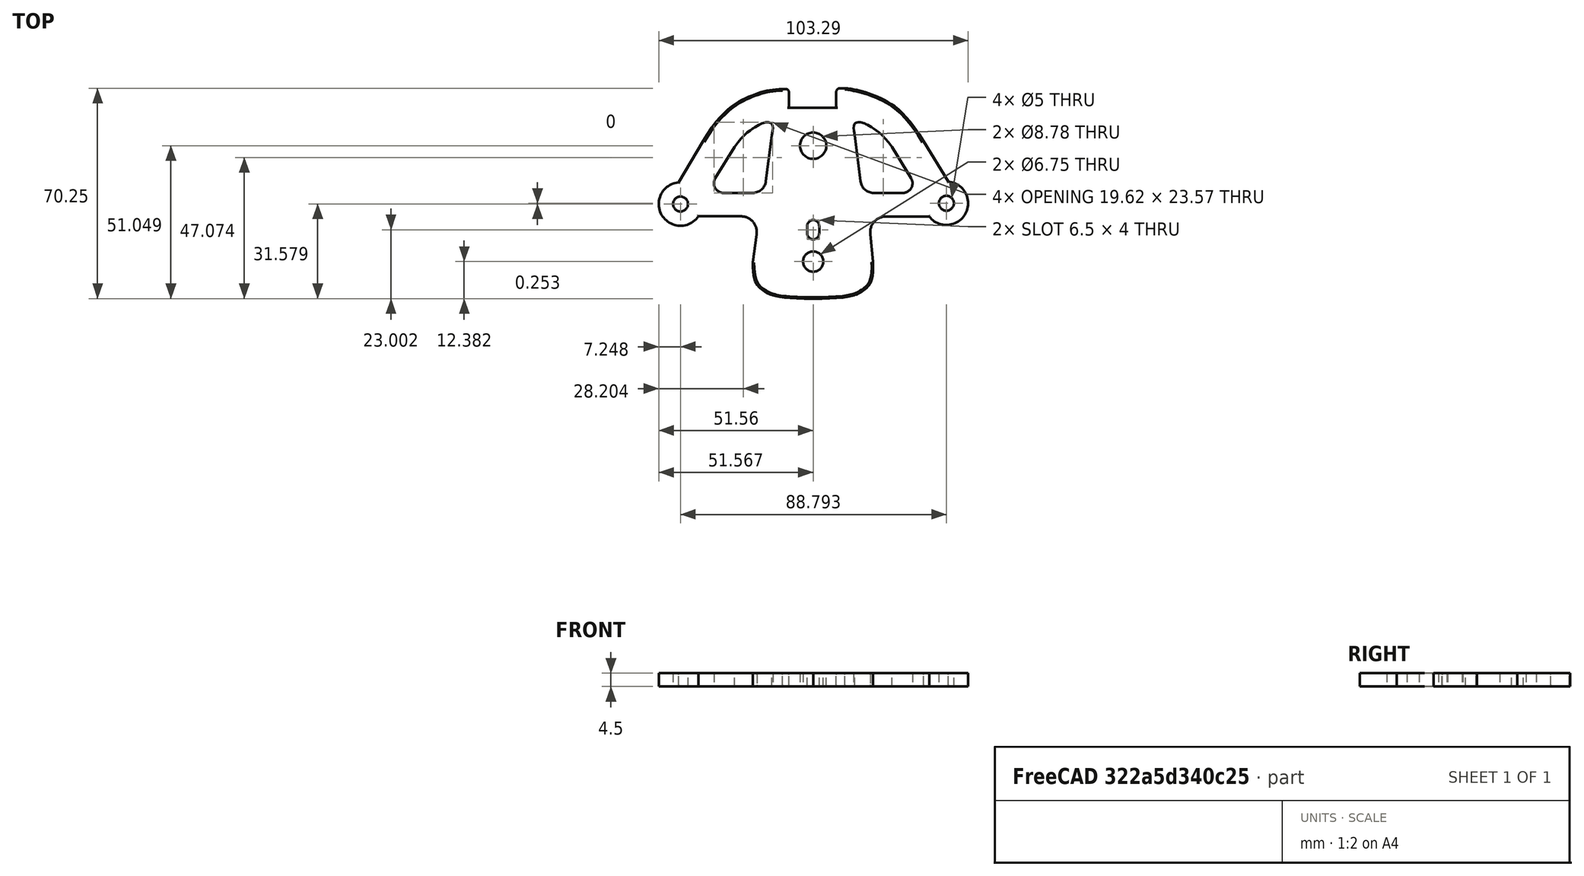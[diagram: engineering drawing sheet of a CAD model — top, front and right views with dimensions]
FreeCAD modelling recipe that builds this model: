
FCSTD DOCUMENT  (FreeCAD 0.20R29603 (Git))
Label: tiller-plate-final
License: Creative Commons Attribution
LicenseURL: http://creativecommons.org/licenses/by/4.0/
objects: Image::ImagePlane×1, Sketcher::SketchObject×1, PartDesign::Pad×1, PartDesign::Body×1, Part::Fillet×1
note: 5 computed .brp shape members not serialized (recipe doc carries the construction recipe); baked Part::Feature solids carry a one-line shape summary decoded from their .brp

FEATURE [Image::ImagePlane] ImagePlane
  Placement = pos=(0.718471,-0.887185,-0.1) rot=(0,0,-1;6.26573rad)
  XSize = 116.42
  YSize = 72.9857
FEATURE [Sketcher::SketchObject] Sketch
  FullyConstrained = false
  MapMode = 5
  Support = -> [XY_Plane]
  sketch-geometry (75):
    g0: ArcOfCircle CenterX=-44.3115 CenterY=-4.63128 CenterZ=0 NormalX=0 NormalY=0 NormalZ=1 AngleXU=0 Radius=7.25 StartAngle=1.65486 EndAngle=5.682
    g1: LineSegment StartX=-8.13082 StartY=27.4789 StartZ=0 EndX=7.6791 EndY=27.4789 EndZ=0
    g2: ArcOfCircle CenterX=44.4815 CenterY=-4.37835 CenterZ=0 NormalX=0 NormalY=0 NormalZ=1 AngleXU=0 Radius=7.25 StartAngle=3.79043 EndAngle=7.77353
    g3-g7: Circle x5 (B-spline internal-alignment scaffolding for g8; pole/knot coordinates omitted)
    g8: BSplineCurve PolesCount=5 KnotsCount=3 Degree=3 IsPeriodic=0
    g9: GeomPoint X=-36.8504 Y=16.2655 Z=0
    g10: GeomPoint X=-22.0365 Y=30.9294 Z=0
    g11: GeomPoint X=-10.281 Y=33.7257 Z=0
    g12: LineSegment StartX=-8.13082 StartY=27.4789 StartZ=0 EndX=-8.13082 EndY=32.8031 EndZ=0
    g13: LineSegment StartX=-10.281 StartY=33.7257 StartZ=0 EndX=-9.05342 EndY=33.7257 EndZ=0
    g14: ArcOfCircle CenterX=-9.05342 CenterY=32.8031 CenterZ=0 NormalX=0 NormalY=0 NormalZ=1 AngleXU=0 Radius=0.922601 StartAngle=2.8e-15 EndAngle=1.5708
    g15: LineSegment StartX=-44.9203 StartY=2.59312 StartZ=0 EndX=-36.8504 EndY=16.2655 EndZ=0
    g16: LineSegment StartX=45.0641 StartY=2.84821 StartZ=0 EndX=36.8504 EndY=16.2655 EndZ=0
    g17: BSplineCurve PolesCount=5 KnotsCount=3 Degree=3 IsPeriodic=0
    g18: Circle CenterX=10.5661 CenterY=34.0385 CenterZ=0 NormalX=0 NormalY=0 NormalZ=1 AngleXU=0 Radius=1
    g19: GeomPoint X=10.5661 Y=34.0385 Z=0
    g20: LineSegment StartX=7.6791 StartY=27.4789 StartZ=0 EndX=7.6791 EndY=32.7332 EndZ=0
    g21: LineSegment StartX=10.5661 StartY=34.0385 StartZ=0 EndX=8.9844 EndY=34.0385 EndZ=0
    g22: ArcOfCircle CenterX=8.9844 CenterY=32.7332 CenterZ=0 NormalX=0 NormalY=0 NormalZ=1 AngleXU=0 Radius=1.3053 StartAngle=1.5708 EndAngle=3.14159
    g23: Circle CenterX=0 CenterY=14.839 CenterZ=0 NormalX=0 NormalY=0 NormalZ=1 AngleXU=0 Radius=4.39
    g24: Circle CenterX=-44.3115 CenterY=-4.63128 CenterZ=0 NormalX=0 NormalY=0 NormalZ=1 AngleXU=0 Radius=2.5
    g25: Circle CenterX=44.4815 CenterY=-4.37835 CenterZ=0 NormalX=0 NormalY=0 NormalZ=1 AngleXU=0 Radius=2.5
    g26: Circle CenterX=0 CenterY=-23.8283 CenterZ=0 NormalX=0 NormalY=0 NormalZ=1 AngleXU=0 Radius=3.375
    g27: LineSegment StartX=-24.1418 StartY=-8.73204 StartZ=0 EndX=-38.3327 EndY=-8.73204 EndZ=0
    g28: LineSegment StartX=-18.8831 StartY=-14.7976 StartZ=0 EndX=-20.2109 EndY=-24.0676 EndZ=0
    g29: ArcOfCircle CenterX=-24.1418 CenterY=-14.0444 CenterZ=0 NormalX=0 NormalY=0 NormalZ=1 AngleXU=0 Radius=5.31234 StartAngle=6.14092 EndAngle=7.85398
    g30: LineSegment StartX=24.3717 StartY=-8.75921 StartZ=0 EndX=38.7048 EndY=-8.75921 EndZ=0
    g31: ArcOfCircle CenterX=24.3717 CenterY=-14.1062 CenterZ=0 NormalX=0 NormalY=0 NormalZ=1 AngleXU=0 Radius=5.34701 StartAngle=1.5708 EndAngle=3.24394
    g32: LineSegment StartX=19.0527 StartY=-14.6525 StartZ=0 EndX=20.0104 EndY=-23.9781 EndZ=0
    g33: LineSegment StartX=-1.99308 StartY=-11.9579 StartZ=0 EndX=-1.99308 EndY=-14.4579 EndZ=0
    g34: ArcOfCircle CenterX=0.00691514 CenterY=-14.4579 CenterZ=0 NormalX=0 NormalY=0 NormalZ=1 AngleXU=0 Radius=2 StartAngle=3.14159 EndAngle=6.28319
    g35: LineSegment StartX=2.00692 StartY=-14.4579 StartZ=0 EndX=2.00692 EndY=-11.9579 EndZ=0
    g36: ArcOfCircle CenterX=0.00691514 CenterY=-11.9579 CenterZ=0 NormalX=0 NormalY=0 NormalZ=1 AngleXU=0 Radius=2 StartAngle=0 EndAngle=3.14159
    g37-g41: Circle x5 (B-spline internal-alignment scaffolding for g42; pole/knot coordinates omitted)
    g42: BSplineCurve PolesCount=5 KnotsCount=3 Degree=3 IsPeriodic=0
    g43: GeomPoint X=-20.2109 Y=-24.0676 Z=0
    g44: GeomPoint X=-16.4959 Y=-33.6189 Z=0
    g45: GeomPoint X=0 Y=-36.2033 Z=0
    g46: BSplineCurve PolesCount=5 KnotsCount=3 Degree=3 IsPeriodic=0
    g47: LineSegment StartX=-13.8688 StartY=18.3787 StartZ=0 EndX=-15.7977 EndY=2.95357 EndZ=0
    g48: LineSegment StartX=-29.9555 StartY=-0.921458 StartZ=0 EndX=-20.1874 EndY=-0.921458 EndZ=0
    g49: ArcOfCircle CenterX=-20.1874 CenterY=3.50249 CenterZ=0 NormalX=0 NormalY=0 NormalZ=1 AngleXU=0 Radius=4.42394 StartAngle=4.71239 EndAngle=6.15879
    g50: LineSegment StartX=-26.3153 StartY=14.4759 StartZ=0 EndX=-32.7012 EndY=3.9578 EndZ=0
    g51: ArcOfCircle CenterX=-29.9555 CenterY=2.29074 CenterZ=0 NormalX=0 NormalY=0 NormalZ=1 AngleXU=0 Radius=3.2122 StartAngle=2.59594 EndAngle=4.71239
    g52-g57: Circle x6 (B-spline internal-alignment scaffolding for g58; pole/knot coordinates omitted)
    g58: BSplineCurve PolesCount=6 KnotsCount=4 Degree=3 IsPeriodic=0
    g59-g62: GeomPoint x4 (B-spline internal-alignment scaffolding for g58; pole/knot coordinates omitted)
    g63: GeomPoint X=0 Y=-23.8283 Z=0
    g64: LineSegment StartX=26.3153 StartY=14.4759 StartZ=0 EndX=32.7012 EndY=3.9578 EndZ=0
    g65: BSplineCurve PolesCount=6 KnotsCount=4 Degree=3 IsPeriodic=0
    g66: LineSegment StartX=13.8688 StartY=18.3787 StartZ=0 EndX=15.7977 EndY=2.95357 EndZ=0
    g67: ArcOfCircle CenterX=20.1874 CenterY=3.50249 CenterZ=0 NormalX=0 NormalY=0 NormalZ=1 AngleXU=0 Radius=4.42394 StartAngle=3.26599 EndAngle=4.71239
    g68: LineSegment StartX=29.9555 StartY=-0.921458 StartZ=0 EndX=20.1874 EndY=-0.921458 EndZ=0
    g69: ArcOfCircle CenterX=29.9555 CenterY=2.29074 CenterZ=0 NormalX=0 NormalY=0 NormalZ=1 AngleXU=0 Radius=3.2122 StartAngle=4.71239 EndAngle=6.82884
    g70: GeomPoint X=-0.103427 Y=-16.4548 Z=0
    g71: GeomPoint X=-0.101997 Y=-20.4548 Z=0
    g72: GeomPoint X=0.0131789 Y=-27.2033 Z=0
    g73: GeomPoint X=-0.00257 Y=27.4789 Z=0
    g74: GeomPoint X=-0.0300529 Y=19.2289 Z=0
  constraints (86):
    c: Radius(g0) = 7.25
    c: Horizontal(g1)
    c: Equal(g2,g0)
    c: Equal(g3, g4-g7) x4
    c: InternalAlignment(g3-g7 -> g8) x5
    c: InternalAlignment(g9,g8)
    c: InternalAlignment(g10,g8)
    c: InternalAlignment(g11,g8)
    c: Coincident(g12,g1)
    c: Coincident(g13,g8)
    c: Horizontal(g13)
    c: Tangent(g12,g14) = -1.5708
    c: Tangent(g13,g14) = 1.5708
    c: Coincident(g15,g8)
    c: InternalAlignment(g18,g17)
    c: InternalAlignment(g19,g17)
    c: Coincident(g21,g17)
    c: Horizontal(g21)
    c: Tangent(g20,g22) = 1.5708
    c: Tangent(g21,g22) = -1.5708
    c: Coincident(g16,g17)
    c: PointOnObject(g23,g-2)
    c: Coincident(g24,g0)
    c: Diameter(g24) = 5
    c: Diameter(g25) = 5
    c: PointOnObject(g26,g-2)
    c: Horizontal(g27)
    c: Tangent(g27,g29) = -1.5708
    c: Tangent(g28,g29) = 1.5708
    c: Horizontal(g30)
    c: Tangent(g30,g31) = 1.5708
    c: Tangent(g32,g31) = -1.5708
    c: Coincident(g2,g25)
    c: Vertical(g33)
    c: Tangent(g33,g34) = -1.5708
    c: Tangent(g34,g35) = -1.5708
    c: Tangent(g35,g36) = -1.5708
    c: Radius(g36) = 2
    c: Equal(g34,g36)
    c: DistanceY(g34,g36) = 2.5
    c: Vertical(g35)
    c: Coincident(g33,g36)
    c: Equal(g37, g38-g41) x4
    c: PointOnObject(g42,g-2)
    c: InternalAlignment(g37-g41 -> g42) x5
    c: InternalAlignment(g43,g42)
    c: InternalAlignment(g44,g42)
    c: InternalAlignment(g45,g42)
    c: Coincident(g28,g42)
    c: Horizontal(g48)
    c: Tangent(g47,g49) = 1.5708
    c: Tangent(g48,g49) = -1.5708
    c: Tangent(g48,g51) = -1.5708
    c: Tangent(g50,g51) = -1.5708
    c: Coincident(g58,g50)
    c: Equal(g52, g53-g57) x5
    c: Coincident(g58,g47)
    c: InternalAlignment(g52-g57 -> g58) x6
    c: InternalAlignment(g59-g62 -> g58) x4
    c: Coincident(g63,g26)
    c: Horizontal(g68)
    c: Tangent(g66,g67) = -1.5708
    c: Tangent(g68,g67) = 1.5708
    c: Tangent(g68,g69) = 1.5708
    c: Tangent(g64,g69) = 1.5708
    c: Coincident(g65,g64)
    c: Coincident(g65,g66)
    c: Coincident(g0,g27)
    c: Coincident(g0,g15)
    c: Coincident(g2,g16)
    c: Coincident(g2,g30)
    c: Coincident(g46,g42)
    c: Vertical(g20)
    c: Vertical(g12)
    c: Coincident(g20,g1)
    c: Coincident(g32,g46)
    c: PointOnObject(g70,g34)
    c: PointOnObject(g71,g26)
    c: DistanceY(g71,g70) = 4
    c: PointOnObject(g72,g26)
    c: DistanceY(g42,g72) = 9
    c: PointOnObject(g73,g1)
    c: PointOnObject(g74,g23)
    c: DistanceY(g74,g73) = 8.25
    c: Diameter(g26) = 6.75
    c: Diameter(g23) = 8.78
FEATURE [PartDesign::Pad] Pad  label="Pad-tiller-plate"
  Direction = (0,0,1)
  Length = 4.5
  Length2 = 10
  Profile = -> Sketch
  ReferenceAxis = -> Sketch [N_Axis]
  Refine = true
  Type = 0
FEATURE [PartDesign::Body] Body  label="Body-tiller-plate"
  Group = -> [Sketch,Pad]
  Origin = -> Origin
  Tip = -> Pad
FEATURE [Part::Fillet] Fillet
  Base = -> Pad
  Edges = 28 edges r=0.5: [Edge3,Edge4,Edge6,Edge7,Edge9,Edge10,Edge12,Edge13,Edge15,Edge16,Edge18,Edge19,Edge21,Edge22,Edge24,Edge25,Edge27,Edge28,Edge30,Edge31,Edge33,Edge34,Edge36,Edge37,Edge39,Edge40,Edge62,Edge63]
